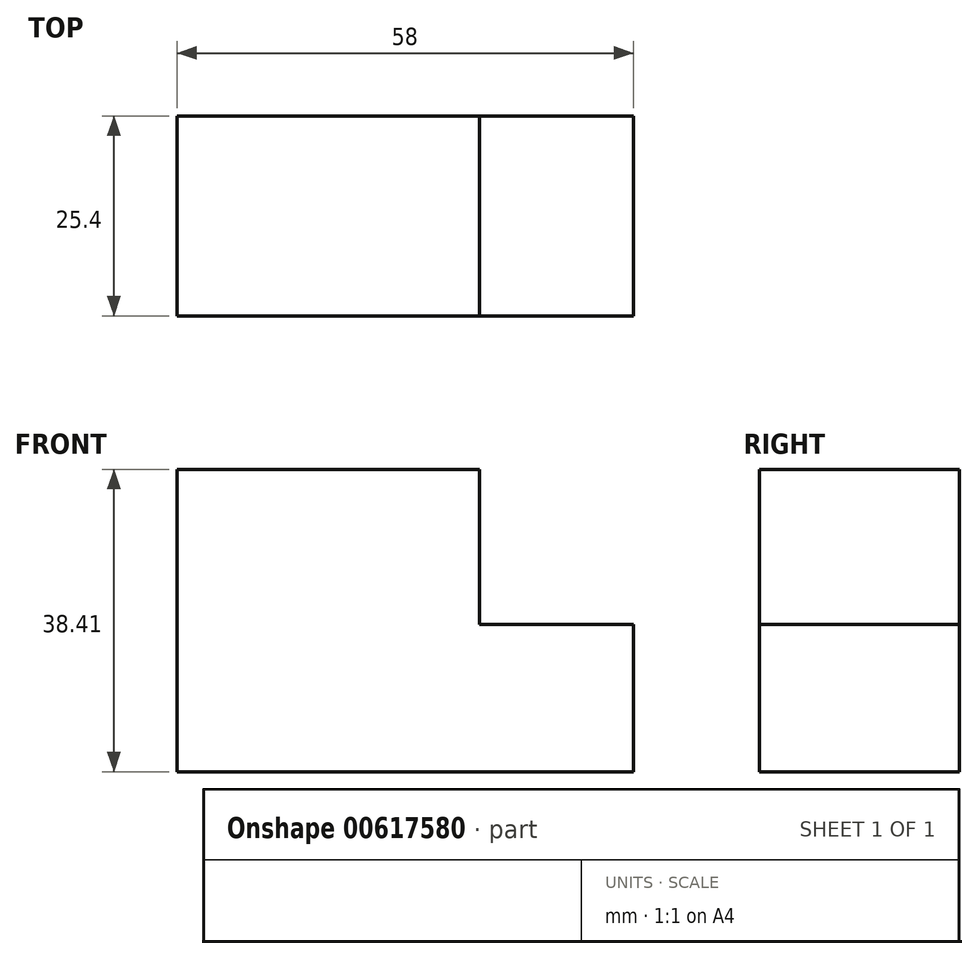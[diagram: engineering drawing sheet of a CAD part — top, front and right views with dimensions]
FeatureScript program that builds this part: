
annotation { "Feature Type Name" : "Feature", "Feature Type Description" : "" }
export const myFeature = defineFeature(function(context is Context, id is Id, definition is map)
    precondition{}
    {
        {
            var Q0;
            Q0=qCreatedBy(makeId("Front.planeOp"),FACE);
            var sketch = newSketch(context, id + "F0", { "sketchPlane" : qUnion([Q0])});
            skLineSegment(sketch, "E0", {"start": v(0, 0) * mm, "end": v(0, 38.4) * mm});
            skLineSegment(sketch, "E1", {"start": v(0, 38.4) * mm, "end": v(38.46, 38.4) * mm});
            skLineSegment(sketch, "E2", {"start": v(38.46, 38.4) * mm, "end": v(38.46, 18.7) * mm});
            skLineSegment(sketch, "E3", {"start": v(38.46, 18.7) * mm, "end": v(58, 18.7) * mm});
            skLineSegment(sketch, "E4", {"start": v(58, 18.7) * mm, "end": v(58, 0) * mm});
            skLineSegment(sketch, "E5", {"start": v(58, 0) * mm, "end": v(0, 0) * mm});
            skSolve(sketch);
        }
        {
            var Q0;
            Q0 = qSketchRegion(id + "F0", true);
            extrude(context, id + "F1", {"entities" : qUnion([Q0]), "depth" : 25.4 * mm, "offsetDistance" : 25.4 * mm});
        }
    });
